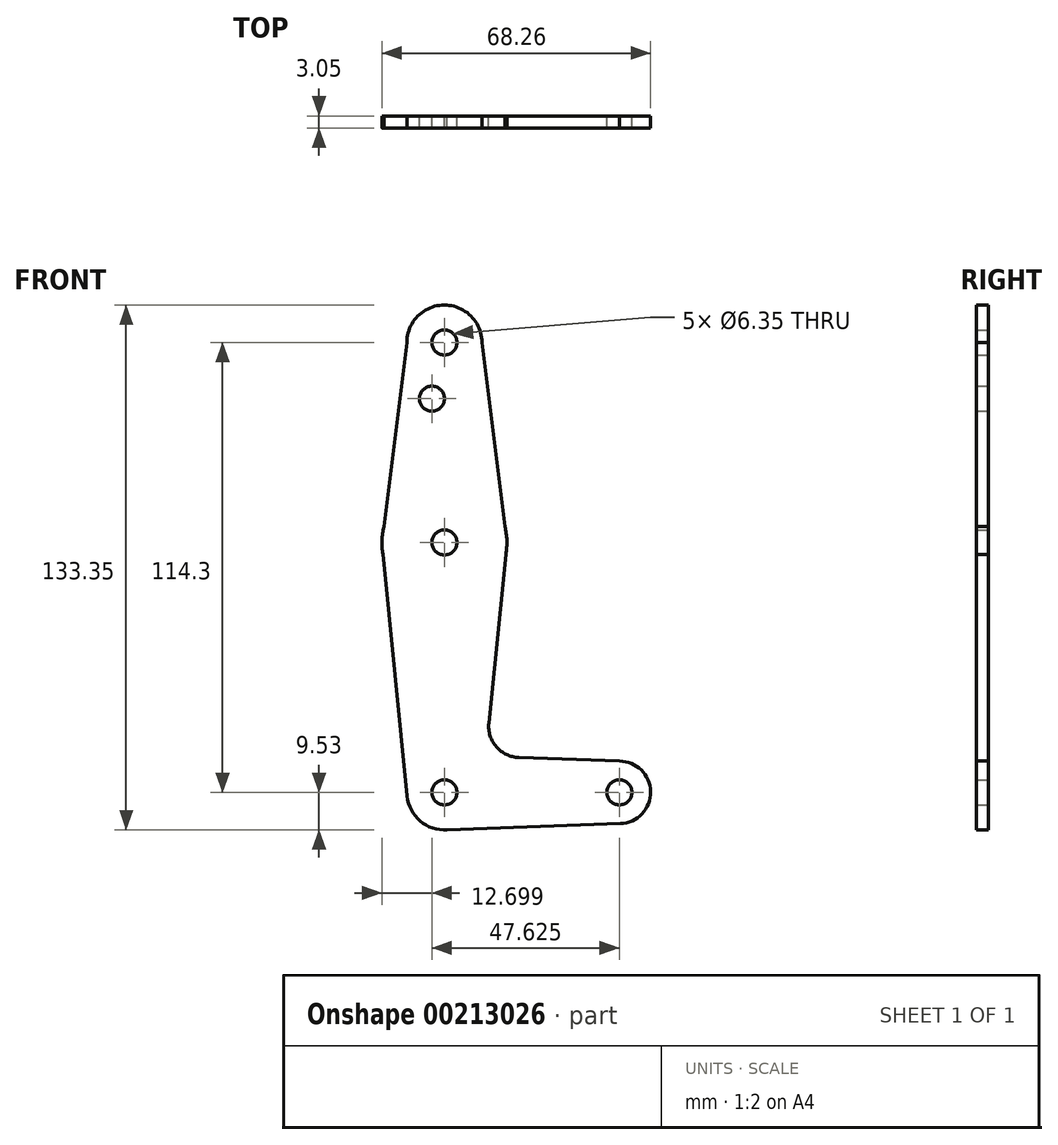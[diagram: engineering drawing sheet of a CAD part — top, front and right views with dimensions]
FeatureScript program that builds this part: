
annotation { "Feature Type Name" : "Feature", "Feature Type Description" : "" }
export const myFeature = defineFeature(function(context is Context, id is Id, definition is map)
    precondition{}
    {
        {
            var Q0;
            Q0=qCreatedBy(makeId("Front.planeOp"),FACE);
            var sketch = newSketch(context, id + "F0", { "sketchPlane" : qUnion([Q0])});
            skLineSegment(sketch, "E0", {"start": v(-21.67, 95.9) * mm, "end": v(-21.67, -18.68) * mm, "construction": true});
            skCircle(sketch, "E1", {"center": v(-21.67, 95.9) * mm, "radius": 9.53 * mm});
            skCircle(sketch, "E2", {"center": v(-21.67, 45.1) * mm, "radius": 15.88 * mm});
            skCircle(sketch, "E3", {"center": v(-21.67, -18.4) * mm, "radius": 9.53 * mm});
            skLineSegment(sketch, "E4", {"start": v(-21.67, -18.4) * mm, "end": v(22.78, -18.4) * mm, "construction": true});
            skCircle(sketch, "E5", {"center": v(22.78, -18.4) * mm, "radius": 7.94 * mm});
            skLineSegment(sketch, "E6", {"start": v(-31.2, 95.87) * mm, "end": v(-37.54, 44.96) * mm});
            skLineSegment(sketch, "E7", {"start": v(-37.54, 44.96) * mm, "end": v(-31.14, -19.34) * mm});
            skLineSegment(sketch, "E8", {"start": v(-21.67, -27.93) * mm, "end": v(23.07, -26.33) * mm});
            skCircle(sketch, "E9", {"center": v(-21.67, 45.1) * mm, "radius": 3.18 * mm});
            skCircle(sketch, "E10", {"center": v(-21.67, -18.4) * mm, "radius": 3.18 * mm});
            skCircle(sketch, "E11", {"center": v(22.78, -18.4) * mm, "radius": 3.18 * mm});
            skCircle(sketch, "E12", {"center": v(-21.67, 95.9) * mm, "radius": 3.18 * mm});
            skPoint(sketch, "E13.newPointA", {"position": v(-21.67, -8.88) * mm});
            skPoint(sketch, "E14", {"position": v(-24.84, 81.62) * mm});
            skCircle(sketch, "E15", {"center": v(-24.84, 81.62) * mm, "radius": 3.18 * mm});
            skLineSegment(sketch, "E16", {"start": v(22.78, -10.46) * mm, "end": v(-2.75, -9.55) * mm});
            skLineSegment(sketch, "E17", {"start": v(-12.14, 95.9) * mm, "end": v(-5.8, 44.96) * mm});
            skLineSegment(sketch, "E18", {"start": v(-5.8, 44.96) * mm, "end": v(-10.38, -0.81) * mm});
            skArc(sketch, "E19.filletArc", {"start": v(-10.38, -0.81) * mm, "mid": v(-8.46, -6.83) * mm, "end": v(-2.75, -9.55) * mm});
            skSolve(sketch);
        }
        {
            var Q0;
            Q0 = qSketchRegion(id + "F0", true);
            extrude(context, id + "F1", {"entities" : qUnion([Q0]), "depth" : 3.05 * mm});
        }
    });
